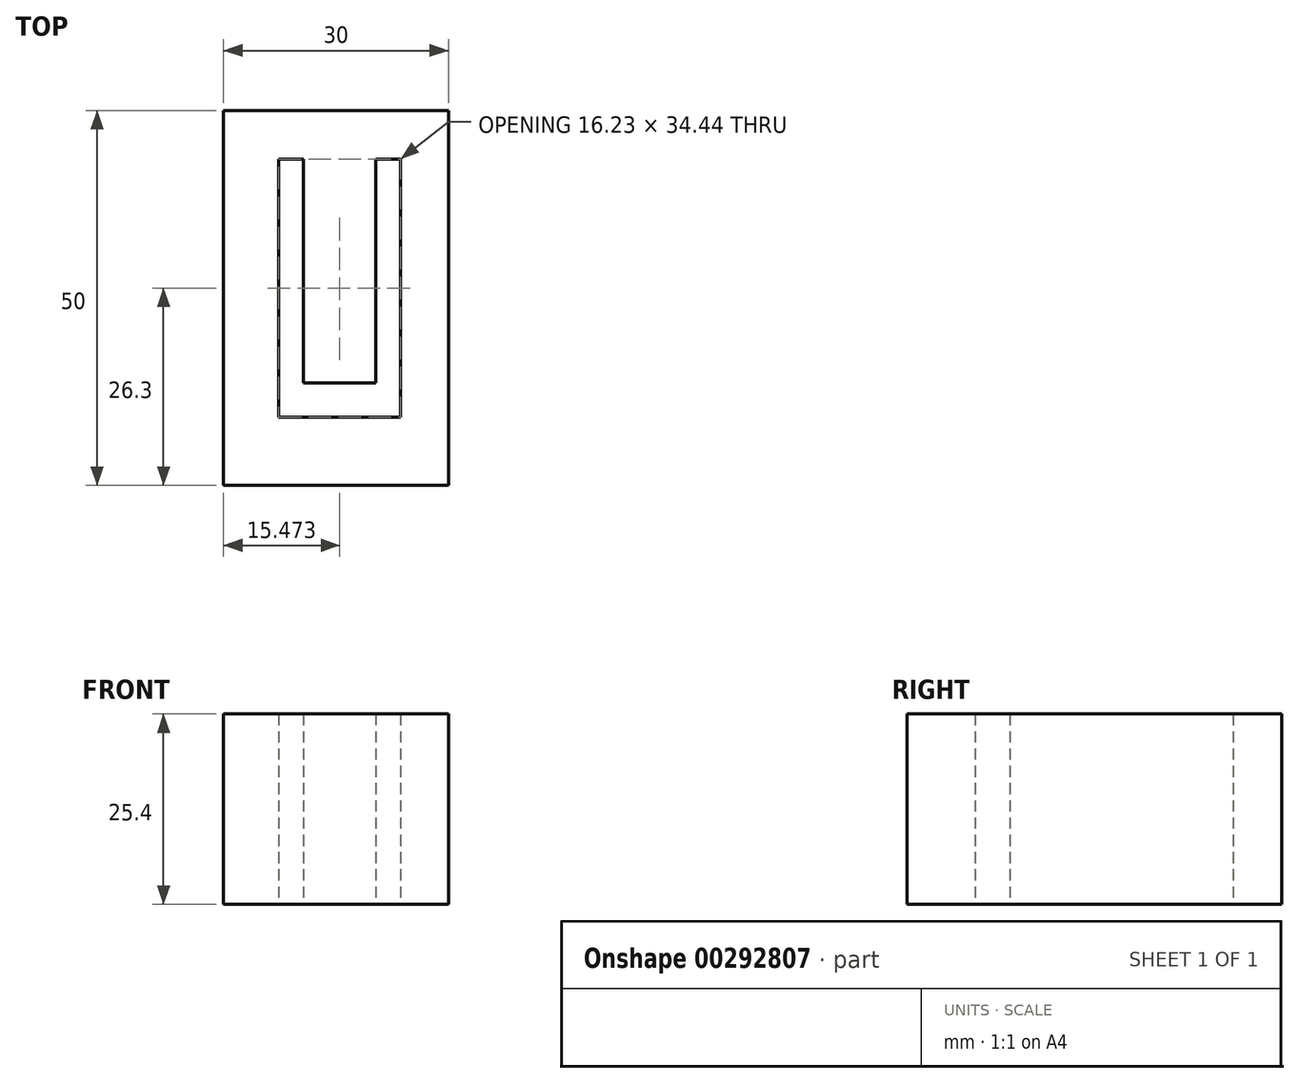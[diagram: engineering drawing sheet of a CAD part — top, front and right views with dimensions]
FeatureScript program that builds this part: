
annotation { "Feature Type Name" : "Feature", "Feature Type Description" : "" }
export const myFeature = defineFeature(function(context is Context, id is Id, definition is map)
    precondition{}
    {
        {
            var Q0;
            Q0=qCreatedBy(makeId("Top.planeOp"),FACE);
            var sketch = newSketch(context, id + "F0", { "sketchPlane" : qUnion([Q0])});
            skLineSegment(sketch, "E0", {"start": v(-36.54, 30.01) * mm, "end": v(-36.54, -19.99) * mm});
            skLineSegment(sketch, "E1", {"start": v(-36.54, -19.99) * mm, "end": v(-6.54, -19.99) * mm});
            skLineSegment(sketch, "E2", {"start": v(-6.54, -19.99) * mm, "end": v(-6.54, 30.01) * mm});
            skLineSegment(sketch, "E3", {"start": v(-6.54, 30.01) * mm, "end": v(-36.54, 30.01) * mm});
            skLineSegment(sketch, "E4", {"start": v(-29.18, 23.53) * mm, "end": v(-29.18, -10.91) * mm});
            skLineSegment(sketch, "E5", {"start": v(-29.18, -10.91) * mm, "end": v(-12.95, -10.91) * mm});
            skLineSegment(sketch, "E6", {"start": v(-12.95, -10.91) * mm, "end": v(-12.95, 23.53) * mm});
            skLineSegment(sketch, "E7", {"start": v(-12.95, 23.53) * mm, "end": v(-16.24, 23.53) * mm});
            skLineSegment(sketch, "E8", {"start": v(-16.24, 23.53) * mm, "end": v(-16.24, -6.3) * mm});
            skLineSegment(sketch, "E9", {"start": v(-16.24, -6.3) * mm, "end": v(-25.9, -6.3) * mm});
            skLineSegment(sketch, "E10", {"start": v(-25.9, -6.3) * mm, "end": v(-25.9, 23.53) * mm});
            skLineSegment(sketch, "E11", {"start": v(-25.9, 23.53) * mm, "end": v(-29.18, 23.53) * mm});
            skSolve(sketch);
        }
        {
            var Q0;
            Q0=makeQuery(id+"F0.imprint","IMPRINT",FACE,{"disambiguationData":[TD([[makeQuery(id+"F0.imprint","IMPRINT",EDGE,{"derivedFrom":sQuery(id+"F0.wireOp",EDGE,"E0")}),1.0]])]});
            extrude(context, id + "F1", {"entities" : qUnion([Q0]), "depth" : 25.4 * mm});
        }
    });
